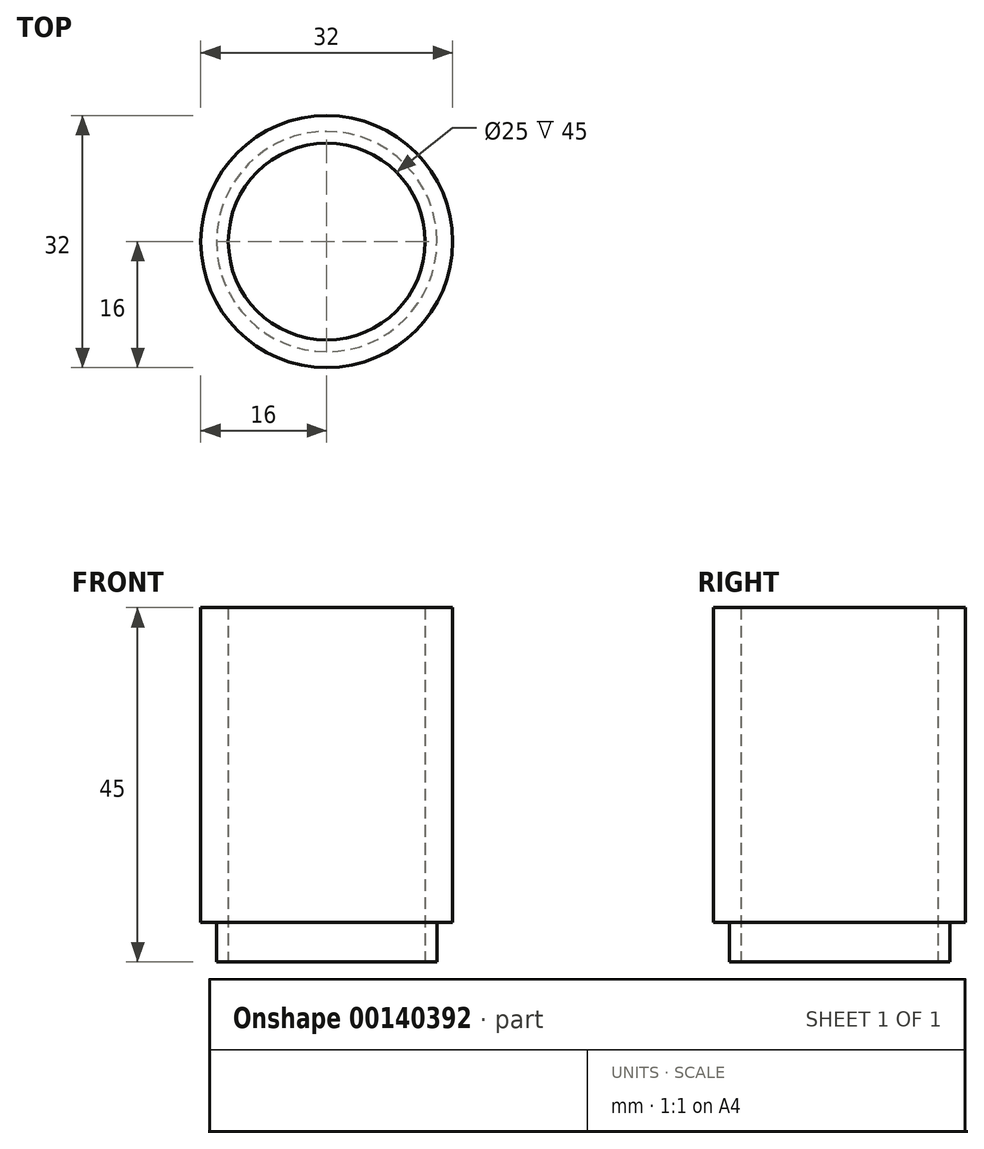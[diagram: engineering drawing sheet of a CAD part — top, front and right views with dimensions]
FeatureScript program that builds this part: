
annotation { "Feature Type Name" : "Feature", "Feature Type Description" : "" }
export const myFeature = defineFeature(function(context is Context, id is Id, definition is map)
    precondition{}
    {
        {
            var Q0;
            Q0=qCreatedBy(makeId("Front.planeOp"),FACE);
            var sketch = newSketch(context, id + "F0", { "sketchPlane" : qUnion([Q0])});
            skLineSegment(sketch, "E0", {"start": v(12.5, 0) * mm, "end": v(14, 0) * mm});
            skLineSegment(sketch, "E1", {"start": v(14, 0) * mm, "end": v(14, 5) * mm});
            skLineSegment(sketch, "E2", {"start": v(14, 5) * mm, "end": v(16, 5) * mm});
            skLineSegment(sketch, "E3", {"start": v(16, 5) * mm, "end": v(16, 45) * mm});
            skLineSegment(sketch, "E4", {"start": v(16, 45) * mm, "end": v(12.5, 45) * mm});
            skLineSegment(sketch, "E5", {"start": v(12.5, 45) * mm, "end": v(12.5, 0) * mm});
            skLineSegment(sketch, "E6", {"start": v(0, 0) * mm, "end": v(0, 43.78) * mm, "construction": true});
            skSolve(sketch);
        }
        {
            var Q0;
            Q0=makeQuery(id+"F0.imprint","IMPRINT",FACE,{"disambiguationData":[TD([[makeQuery(id+"F0.imprint","IMPRINT",EDGE,{"derivedFrom":sQuery(id+"F0.wireOp",EDGE,"E0")}),1.0]])]});
            var Q1;
            Q1=sQuery(id+"F0.wireOp",EDGE,"E6");
            revolve(context, id + "F1", {"entities" : qUnion([Q0]), "axis" : qUnion([Q1]), "revolveType" : RevolveType.FULL});
        }
    });
